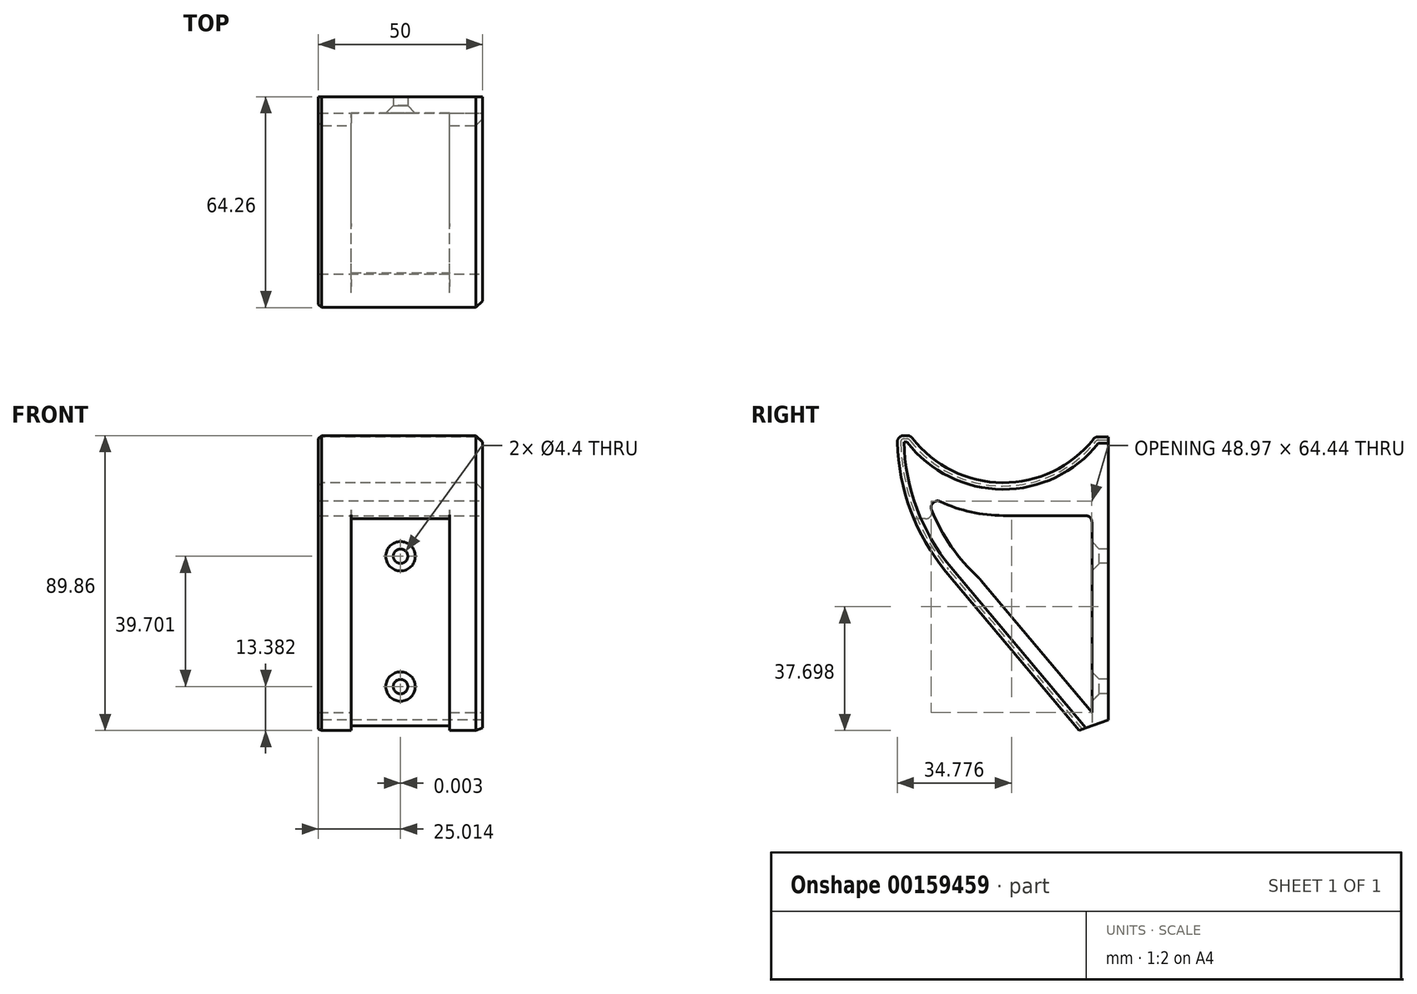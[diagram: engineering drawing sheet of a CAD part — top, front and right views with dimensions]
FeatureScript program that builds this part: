
annotation { "Feature Type Name" : "Feature", "Feature Type Description" : "" }
export const myFeature = defineFeature(function(context is Context, id is Id, definition is map)
    precondition{}
    {
        {
            var Q0;
            Q0=qCreatedBy(makeId("Right.planeOp"),FACE);
            var sketch = newSketch(context, id + "F0", { "sketchPlane" : qUnion([Q0])});
            skLineSegment(sketch, "E0", {"start": v(0, 0) * mm, "end": v(0, 100) * mm});
            skArc(sketch, "E1", {"start": v(-4, 100) * mm, "mid": v(-32.23, 86) * mm, "end": v(-60.28, 100.38) * mm});
            skLineSegment(sketch, "E2", {"start": v(-4, 100) * mm, "end": v(0, 100) * mm});
            skArc(sketch, "E3", {"start": v(-49.5, 58.98) * mm, "mid": v(-60.54, 78.38) * mm, "end": v(-64.28, 100.39) * mm});
            skLineSegment(sketch, "E4", {"start": v(-49.5, 58.98) * mm, "end": v(0, 0) * mm});
            skLineSegment(sketch, "E5", {"start": v(-64.28, 100.39) * mm, "end": v(-60.28, 100.38) * mm});
            skSolve(sketch);
        }
        {
            var Q0;
            Q0=makeQuery(id+"F0.imprint","IMPRINT",FACE,{"disambiguationData":[TD([[makeQuery(id+"F0.imprint","IMPRINT",EDGE,{"derivedFrom":sQuery(id+"F0.wireOp",EDGE,"E0")}),1.0]])]});
            extrude(context, id + "F1", {"entities" : qUnion([Q0]), "depth" : 50 * mm});
        }
        {
            var Q0;
            Q0=qCreatedBy(makeId("Right.planeOp"),FACE);
            cPlane(context, id + "F2", {"entities" : qUnion([Q0]), "cplaneType" : CPlaneType.OFFSET, "offset" : 25 * mm, "width" : 150 * mm, "height" : 150 * mm});
        }
        {
            var Q0;
            Q0=qCreatedBy(id+"F2.planeOp",FACE);
            var sketch = newSketch(context, id + "F3", { "sketchPlane" : qUnion([Q0])});
            skPoint(sketch, "E6", {"position": v(-32, 121) * mm});
            skArc(sketch, "E7", {"start": v(-55.6, 82.68) * mm, "mid": v(-44.26, 77.7) * mm, "end": v(-32, 76) * mm});
            skLineSegment(sketch, "E8", {"start": v(-32, 76) * mm, "end": v(-5, 76) * mm});
            skLineSegment(sketch, "E9", {"start": v(-5, 76) * mm, "end": v(-5, 16) * mm});
            skLineSegment(sketch, "E10", {"start": v(-5, 16) * mm, "end": v(-39.08, 56.61) * mm});
            skArc(sketch, "E11", {"start": v(-55.6, 82.68) * mm, "mid": v(-49.1, 68.53) * mm, "end": v(-39.08, 56.61) * mm});
            skSolve(sketch);
        }
        {
            var Q0;
            Q0 = qSketchRegion(id + "F3", true);
            extrude(context, id + "F4", {"entities" : qUnion([Q0]), "operationType" : NewBodyOperationType.REMOVE, "endBound" : BoundingType.SYMMETRIC, "oppositeDirection" : true, "depth" : 50 * mm});
        }
        {
            var Q0;
            Q0=qCreatedBy(makeId("Top.planeOp"),FACE);
            var sketch = newSketch(context, id + "F5", { "sketchPlane" : qUnion([Q0])});
            skLineSegment(sketch, "E12.bottom", {"start": v(10, -5) * mm, "end": v(40, -5) * mm});
            skLineSegment(sketch, "E12.top", {"start": v(10, -65) * mm, "end": v(40, -65) * mm});
            skLineSegment(sketch, "E12.left", {"start": v(10, -5) * mm, "end": v(10, -65) * mm});
            skLineSegment(sketch, "E12.right", {"start": v(40, -5) * mm, "end": v(40, -65) * mm});
            skSolve(sketch);
        }
        {
            var Q0;
            Q0 = qSketchRegion(id + "F5", true);
            extrude(context, id + "F6", {"entities" : qUnion([Q0]), "operationType" : NewBodyOperationType.REMOVE, "depth" : 75 * mm});
        }
        {
            var Q0;
            Q0=makeQuery(id+"F6.boolean.opBoolean","MERGE",FACE,{"derivedFrom":[makeQuery(id+"F4.boolean.opBoolean","COPY",FACE,{"derivedFrom":makeQuery(id+"F4.opExtrude","SWEPT_FACE",FACE,{"disambiguationData":[OSD([sQuery(id+"F3.wireOp",EDGE,"E9")])]})}),makeQuery(id+"F6.opExtrude","SWEPT_FACE",FACE,{"disambiguationData":[OSD([sQuery(id+"F5.wireOp",EDGE,"E12.bottom")])]})]});
            var sketch = newSketch(context, id + "F7", { "sketchPlane" : qUnion([Q0])});
            skPoint(sketch, "E13", {"position": v(25.01, 63.6) * mm});
            skPoint(sketch, "E14", {"position": v(25.02, 23.9) * mm});
            skSolve(sketch);
        }
        {
            var Q0;
            Q0=sQuery(id+"F7.wireOp",VERTEX,"E13");
            var Q1;
            Q1=sQuery(id+"F7.wireOp",VERTEX,"E14");
            var Q2;
            Q2=makeQuery(id+"F1.opExtrude","SWEPT_BODY",BODY,{"disambiguationData":[OSD([sQuery(id+"F0.wireOp",EDGE,"E0"),sQuery(id+"F0.wireOp",EDGE,"E1"),sQuery(id+"F0.wireOp",EDGE,"E2"),sQuery(id+"F0.wireOp",EDGE,"E3"),sQuery(id+"F0.wireOp",EDGE,"E4"),sQuery(id+"F0.wireOp",EDGE,"E5")])]});
            hole(context, id + "F8", {"style" : HoleStyle.C_SINK, "endStyle" : HoleEndStyle.THROUGH, "standardTappedOrClearance" : lookupTablePath({ "standard" : "ISO", "fit" : "Normal", "size" : "M4", "type" : "Clearance" }), "standardBlindInLast" : lookupTablePath({ "fit" : "Standard", "standard" : "ISO", "size" : "M4", "type" : "Clearance" }), "holeDiameter" : 4.4 * mm, "cSinkDiameter" : 8.96 * mm, "cSinkAngle" : 90 * degree, "locations" : qUnion([Q0, Q1]), "scope" : qUnion([Q2]), "isTappedThrough" : true});
        }
        {
            var Q0;
            Q0=makeQuery(id+"F1.opExtrude","SWEPT_EDGE",EDGE,{"disambiguationData":[OSD([sQuery(id+"F0.wireOp",EDGE,"E3"),sQuery(id+"F0.wireOp",EDGE,"E5")])]});
            var Q1;
            Q1=makeQuery(id+"F1.opExtrude","SWEPT_EDGE",EDGE,{"disambiguationData":[OSD([sQuery(id+"F0.wireOp",EDGE,"E1"),sQuery(id+"F0.wireOp",EDGE,"E5")])]});
            var Q2;
            Q2=makeQuery(id+"F1.opExtrude","SWEPT_EDGE",EDGE,{"disambiguationData":[OSD([sQuery(id+"F0.wireOp",EDGE,"E1"),sQuery(id+"F0.wireOp",EDGE,"E2")])]});
            var Q3;
            Q3=makeQuery(id+"F6.boolean.opBoolean","INTERSECT",EDGE,{"derivedFrom":[makeQuery(id+"F1.opExtrude","SWEPT_FACE",FACE,{"disambiguationData":[OSD([sQuery(id+"F0.wireOp",EDGE,"E3")])]}),makeQuery(id+"F6.opExtrude","CAP_FACE",FACE,{"disambiguationData":[OSD([sQuery(id+"F5.wireOp",EDGE,"E12.bottom"),sQuery(id+"F5.wireOp",EDGE,"E12.top"),sQuery(id+"F5.wireOp",EDGE,"E12.left"),sQuery(id+"F5.wireOp",EDGE,"E12.right")])],"isStart":false})]});
            var Q4;
            Q4=makeQuery(id+"F4.boolean.opBoolean","COPY",EDGE,{"derivedFrom":makeQuery(id+"F4.opExtrude","SWEPT_EDGE",EDGE,{"disambiguationData":[OSD([sQuery(id+"F3.wireOp",EDGE,"E7"),sQuery(id+"F3.wireOp",EDGE,"E11")])]})});
            var Q5;
            Q5=makeQuery(id+"F4.boolean.opBoolean","COPY",EDGE,{"derivedFrom":makeQuery(id+"F4.opExtrude","SWEPT_EDGE",EDGE,{"disambiguationData":[OSD([sQuery(id+"F3.wireOp",EDGE,"E8"),sQuery(id+"F3.wireOp",EDGE,"E9")])]})});
            fillet(context, id + "F9", {"entities" : qUnion([Q0, Q1, Q2, Q3, Q4, Q5]), "radius" : 2 * mm, "tangentPropagation" : true, "allowEdgeOverflow" : false});
        }
        {
            var Q0;
            Q0=makeQuery(id+"F6.boolean.opBoolean","INTERSECT",EDGE,{"derivedFrom":[makeQuery(id+"F4.boolean.opBoolean","COPY",FACE,{"derivedFrom":makeQuery(id+"F4.opExtrude","SWEPT_FACE",FACE,{"disambiguationData":[OSD([sQuery(id+"F3.wireOp",EDGE,"E11")])]})}),makeQuery(id+"F6.opExtrude","CAP_FACE",FACE,{"disambiguationData":[OSD([sQuery(id+"F5.wireOp",EDGE,"E12.bottom"),sQuery(id+"F5.wireOp",EDGE,"E12.top"),sQuery(id+"F5.wireOp",EDGE,"E12.left"),sQuery(id+"F5.wireOp",EDGE,"E12.right")])],"isStart":false})]});
            fillet(context, id + "F10", {"entities" : qUnion([Q0]), "radius" : 2 * mm, "tangentPropagation" : true, "allowEdgeOverflow" : false});
        }
        {
            var Q0;
            {var subQ0=sQuery(id+"F3.wireOp",EDGE,"E10");var subQ1=sQuery(id+"F3.wireOp",EDGE,"E11");Q0=makeQuery(id+"F6.boolean.opBoolean","SPLIT",EDGE,{"disambiguationData":[TD([makeQuery(id+"F6.opExtrude","SWEPT_FACE",FACE,{"disambiguationData":[OSD([sQuery(id+"F5.wireOp",EDGE,"E12.right")])]})])],"derivedFrom":makeQuery(id+"F4.boolean.opBoolean","COPY",EDGE,{"derivedFrom":makeQuery(id+"F4.opExtrude","SWEPT_EDGE",EDGE,{"disambiguationData":[OSD([subQ0,subQ1])]})})});}
            var Q1;
            {var subQ0=sQuery(id+"F3.wireOp",EDGE,"E11");var subQ1=sQuery(id+"F3.wireOp",EDGE,"E10");Q1=makeQuery(id+"F6.boolean.opBoolean","SPLIT",EDGE,{"disambiguationData":[TD([makeQuery(id+"F6.opExtrude","SWEPT_FACE",FACE,{"disambiguationData":[OSD([sQuery(id+"F5.wireOp",EDGE,"E12.left")])]})])],"derivedFrom":makeQuery(id+"F4.boolean.opBoolean","COPY",EDGE,{"derivedFrom":makeQuery(id+"F4.opExtrude","SWEPT_EDGE",EDGE,{"disambiguationData":[OSD([subQ1,subQ0])]})})});}
            fillet(context, id + "F11", {"entities" : qUnion([Q0, Q1]), "radius" : 10 * mm, "tangentPropagation" : true, "allowEdgeOverflow" : false});
        }
        {
            var Q0;
            Q0=makeQuery(id+"F1.opExtrude","CAP_EDGE",EDGE,{"disambiguationData":[OSD([sQuery(id+"F0.wireOp",EDGE,"E1")])],"isStart":false});
            var Q1;
            Q1=makeQuery(id+"F1.opExtrude","CAP_EDGE",EDGE,{"disambiguationData":[OSD([sQuery(id+"F0.wireOp",EDGE,"E3")])],"isStart":false});
            var Q2;
            {var subQ0=sQuery(id+"F0.wireOp",EDGE,"E5");var subQ1=sQuery(id+"F0.wireOp",EDGE,"E3");Q2=makeQuery(id+"F9.opFillet","BLEND_EDGE",EDGE,{"blendedFrom":[makeQuery(id+"F1.opExtrude","SWEPT_EDGE",EDGE,{"disambiguationData":[OSD([subQ1,subQ0])]}),makeQuery(id+"F1.opExtrude","CAP_FACE",FACE,{"disambiguationData":[OSD([sQuery(id+"F0.wireOp",EDGE,"E0"),sQuery(id+"F0.wireOp",EDGE,"E1"),sQuery(id+"F0.wireOp",EDGE,"E2"),subQ1,sQuery(id+"F0.wireOp",EDGE,"E4"),subQ0])],"isStart":false})],"blendedInto":[makeQuery(id+"F1.opExtrude","CAP_FACE",FACE,{"disambiguationData":[OSD([sQuery(id+"F0.wireOp",EDGE,"E0"),sQuery(id+"F0.wireOp",EDGE,"E1"),sQuery(id+"F0.wireOp",EDGE,"E2"),subQ1,sQuery(id+"F0.wireOp",EDGE,"E4"),subQ0])],"isStart":false})]});}
            var Q3;
            Q3=makeQuery(id+"F1.opExtrude","CAP_EDGE",EDGE,{"disambiguationData":[OSD([sQuery(id+"F0.wireOp",EDGE,"E5")])],"isStart":false});
            var Q4;
            {var subQ0=sQuery(id+"F0.wireOp",EDGE,"E5");var subQ1=sQuery(id+"F0.wireOp",EDGE,"E1");Q4=makeQuery(id+"F9.opFillet","BLEND_EDGE",EDGE,{"blendedFrom":[makeQuery(id+"F1.opExtrude","SWEPT_EDGE",EDGE,{"disambiguationData":[OSD([subQ1,subQ0])]}),makeQuery(id+"F1.opExtrude","CAP_FACE",FACE,{"disambiguationData":[OSD([sQuery(id+"F0.wireOp",EDGE,"E0"),subQ1,sQuery(id+"F0.wireOp",EDGE,"E2"),sQuery(id+"F0.wireOp",EDGE,"E3"),sQuery(id+"F0.wireOp",EDGE,"E4"),subQ0])],"isStart":false})],"blendedInto":[makeQuery(id+"F1.opExtrude","CAP_FACE",FACE,{"disambiguationData":[OSD([sQuery(id+"F0.wireOp",EDGE,"E0"),subQ1,sQuery(id+"F0.wireOp",EDGE,"E2"),sQuery(id+"F0.wireOp",EDGE,"E3"),sQuery(id+"F0.wireOp",EDGE,"E4"),subQ0])],"isStart":false})]});}
            var Q5;
            {var subQ0=sQuery(id+"F0.wireOp",EDGE,"E2");var subQ1=sQuery(id+"F0.wireOp",EDGE,"E1");Q5=makeQuery(id+"F9.opFillet","BLEND_EDGE",EDGE,{"blendedFrom":[makeQuery(id+"F1.opExtrude","SWEPT_EDGE",EDGE,{"disambiguationData":[OSD([subQ1,subQ0])]}),makeQuery(id+"F1.opExtrude","CAP_FACE",FACE,{"disambiguationData":[OSD([sQuery(id+"F0.wireOp",EDGE,"E0"),subQ1,subQ0,sQuery(id+"F0.wireOp",EDGE,"E3"),sQuery(id+"F0.wireOp",EDGE,"E4"),sQuery(id+"F0.wireOp",EDGE,"E5")])],"isStart":false})],"blendedInto":[makeQuery(id+"F1.opExtrude","CAP_FACE",FACE,{"disambiguationData":[OSD([sQuery(id+"F0.wireOp",EDGE,"E0"),subQ1,subQ0,sQuery(id+"F0.wireOp",EDGE,"E3"),sQuery(id+"F0.wireOp",EDGE,"E4"),sQuery(id+"F0.wireOp",EDGE,"E5")])],"isStart":false})]});}
            var Q6;
            Q6=makeQuery(id+"F1.opExtrude","CAP_EDGE",EDGE,{"disambiguationData":[OSD([sQuery(id+"F0.wireOp",EDGE,"E2")])],"isStart":false});
            var Q7;
            Q7=makeQuery(id+"F1.opExtrude","CAP_EDGE",EDGE,{"disambiguationData":[OSD([sQuery(id+"F0.wireOp",EDGE,"E4")])],"isStart":false});
            chamfer(context, id + "F12", {"entities" : qUnion([Q0, Q1, Q2, Q3, Q4, Q5, Q6, Q7]), "width" : 2 * mm, "tangentPropagation" : true});
        }
        {
            var Q0;
            Q0=makeQuery(id+"F1.opExtrude","CAP_EDGE",EDGE,{"disambiguationData":[OSD([sQuery(id+"F0.wireOp",EDGE,"E2")])],"isStart":true});
            var Q1;
            {var subQ0=sQuery(id+"F0.wireOp",EDGE,"E2");var subQ1=sQuery(id+"F0.wireOp",EDGE,"E1");Q1=makeQuery(id+"F9.opFillet","BLEND_EDGE",EDGE,{"blendedFrom":[makeQuery(id+"F1.opExtrude","SWEPT_EDGE",EDGE,{"disambiguationData":[OSD([subQ1,subQ0])]}),makeQuery(id+"F1.opExtrude","CAP_FACE",FACE,{"disambiguationData":[OSD([sQuery(id+"F0.wireOp",EDGE,"E0"),subQ1,subQ0,sQuery(id+"F0.wireOp",EDGE,"E3"),sQuery(id+"F0.wireOp",EDGE,"E4"),sQuery(id+"F0.wireOp",EDGE,"E5")])],"isStart":true})],"blendedInto":[makeQuery(id+"F1.opExtrude","CAP_FACE",FACE,{"disambiguationData":[OSD([sQuery(id+"F0.wireOp",EDGE,"E0"),subQ1,subQ0,sQuery(id+"F0.wireOp",EDGE,"E3"),sQuery(id+"F0.wireOp",EDGE,"E4"),sQuery(id+"F0.wireOp",EDGE,"E5")])],"isStart":true})]});}
            var Q2;
            Q2=makeQuery(id+"F1.opExtrude","CAP_EDGE",EDGE,{"disambiguationData":[OSD([sQuery(id+"F0.wireOp",EDGE,"E1")])],"isStart":true});
            var Q3;
            {var subQ0=sQuery(id+"F0.wireOp",EDGE,"E5");var subQ1=sQuery(id+"F0.wireOp",EDGE,"E1");Q3=makeQuery(id+"F9.opFillet","BLEND_EDGE",EDGE,{"blendedFrom":[makeQuery(id+"F1.opExtrude","SWEPT_EDGE",EDGE,{"disambiguationData":[OSD([subQ1,subQ0])]}),makeQuery(id+"F1.opExtrude","CAP_FACE",FACE,{"disambiguationData":[OSD([sQuery(id+"F0.wireOp",EDGE,"E0"),subQ1,sQuery(id+"F0.wireOp",EDGE,"E2"),sQuery(id+"F0.wireOp",EDGE,"E3"),sQuery(id+"F0.wireOp",EDGE,"E4"),subQ0])],"isStart":true})],"blendedInto":[makeQuery(id+"F1.opExtrude","CAP_FACE",FACE,{"disambiguationData":[OSD([sQuery(id+"F0.wireOp",EDGE,"E0"),subQ1,sQuery(id+"F0.wireOp",EDGE,"E2"),sQuery(id+"F0.wireOp",EDGE,"E3"),sQuery(id+"F0.wireOp",EDGE,"E4"),subQ0])],"isStart":true})]});}
            var Q4;
            Q4=makeQuery(id+"F1.opExtrude","CAP_EDGE",EDGE,{"disambiguationData":[OSD([sQuery(id+"F0.wireOp",EDGE,"E5")])],"isStart":true});
            var Q5;
            {var subQ0=sQuery(id+"F0.wireOp",EDGE,"E5");var subQ1=sQuery(id+"F0.wireOp",EDGE,"E3");Q5=makeQuery(id+"F9.opFillet","BLEND_EDGE",EDGE,{"blendedFrom":[makeQuery(id+"F1.opExtrude","SWEPT_EDGE",EDGE,{"disambiguationData":[OSD([subQ1,subQ0])]}),makeQuery(id+"F1.opExtrude","CAP_FACE",FACE,{"disambiguationData":[OSD([sQuery(id+"F0.wireOp",EDGE,"E0"),sQuery(id+"F0.wireOp",EDGE,"E1"),sQuery(id+"F0.wireOp",EDGE,"E2"),subQ1,sQuery(id+"F0.wireOp",EDGE,"E4"),subQ0])],"isStart":true})],"blendedInto":[makeQuery(id+"F1.opExtrude","CAP_FACE",FACE,{"disambiguationData":[OSD([sQuery(id+"F0.wireOp",EDGE,"E0"),sQuery(id+"F0.wireOp",EDGE,"E1"),sQuery(id+"F0.wireOp",EDGE,"E2"),subQ1,sQuery(id+"F0.wireOp",EDGE,"E4"),subQ0])],"isStart":true})]});}
            var Q6;
            Q6=makeQuery(id+"F1.opExtrude","CAP_EDGE",EDGE,{"disambiguationData":[OSD([sQuery(id+"F0.wireOp",EDGE,"E3")])],"isStart":true});
            var Q7;
            Q7=makeQuery(id+"F1.opExtrude","CAP_EDGE",EDGE,{"disambiguationData":[OSD([sQuery(id+"F0.wireOp",EDGE,"E4")])],"isStart":true});
            chamfer(context, id + "F13", {"entities" : qUnion([Q0, Q1, Q2, Q3, Q4, Q5, Q6, Q7]), "width" : 1 * mm, "tangentPropagation" : true});
        }
        {
            var Q0;
            Q0=makeQuery(id+"F1.opExtrude","SWEPT_EDGE",EDGE,{"disambiguationData":[OSD([sQuery(id+"F0.wireOp",EDGE,"E0"),sQuery(id+"F0.wireOp",EDGE,"E4")])]});
            chamfer(context, id + "F14", {"entities" : qUnion([Q0]), "width" : 5 * mm, "tangentPropagation" : true});
        }
    });
